# Revit family: TopVent_TC
name_source: partatom
category: Mechanical Equipment
revit_build: Autodesk Revit MEP 2015 (Build: 20160512_0715(x64)
units: mm (PartAtom-declared; Revit-internal decimal feet)

## types (3) — shared parameters
COBIE Connected load = 1.5 kW
COBIE Current consumption max. = 2.9A
COBIE Extract air temperature max. = 50°C
COBIE Floor area covered = 537.0
COBIE Frequency = 50 Hz
COBIE Nominal air flow rate = 6000.0
COBIE Octave sound power level - 1000 Hz = 74 dB
COBIE Octave sound power level - 125 Hz = 60 dB
COBIE Octave sound power level - 2000 Hz = 70 dB
COBIE Octave sound power level - 250 Hz = 65 dB
COBIE Octave sound power level - 4000 Hz = 64 dB
COBIE Octave sound power level - 500 Hz = 70 dB
COBIE Octave sound power level - 63 Hz = 55 dB
COBIE Octave sound power level - 8000 Hz = 56 dB
COBIE Permitted voltage tolerance = +/-5%
COBIE Pressure of the heating medium max. = 800 kPa
COBIE Protection rating = IP 54
COBIE Series fuse = 13A
COBIE Sound pressure level (at a distance of 5 m) = 55 dB(A)
COBIE Static efficiency of the fans = 48.5%
COBIE Supply air temperature max. = 60°C
COBIE Supply voltage = 3x400 V AC
COBIE Temperature of the heating medium max. = 90°C
COBIE Total sound power level = 77 dB(A)
Connected load = 3.6 kW
Current consumption max. = 5.9A
Extract air temperature max. = 50°C
Frequency = 50 Hz
M = 25 mm  [stored 0.082021 ft]
Permitted voltage tolerance = +/-5%
Pressure of the heating medium max. = 800 kPa
Protection rating = IP 54
Series fuse = 13A
Supply air temperature max. = 60°C
Supply voltage = 3x400 V AC
Temperature of the heating medium max. = 90°C

## per-type parameters (varying)
- TC-6-C: (X)=850 mm  [stored 2.78871 ft]; A=900 mm  [stored 2.95276 ft]; Air flow rate=3100 m3/h; B=1344 mm  [stored 4.40945 ft]; COBIE Air flow rate=3100 m3/h; COBIE Condensate quantity=90 kg/h; COBIE Condensate quantity 22 °C (50/70 %) - 6/12 °C=0.0/13.5 kg/h; COBIE Condensate quantity 22 °C (50/70 %) - 8/14 °C=0.0/7.9 kg/h; COBIE Condensate quantity 26 °C (50/70 %) - 6/12 °C=8.6/30.2 kg/h; COBIE Condensate quantity 26 °C (50/70 %) - 8/14 °C=3.0/24.6 kg/h; COBIE Effective electric power input=0.46 kW; COBIE Heat output 16/20 °C (60/40 °C)=18.8/16.2 kW; COBIE Heat output 16/20 °C (80/60 °C)=32.8/30.3 kW; COBIE Maximum mounting height 16/20 °C (60/40 °C)=16.8/17.9 m; COBIE Maximum mounting height 16/20 °C (80/60 °C)=13.4/14.0 m; COBIE Sensible cooling capacity 22 °C (50/70 %) - 6/12 °C=20.4/18.5 kW; COBIE Sensible cooling capacity 22 °C (50/70 %) - 8/14 °C=18.0/16.0 kW; COBIE Sensible cooling capacity 26 °C (50/70 %) - 6/12 °C=25.2/23.2 kW; COBIE Sensible cooling capacity 26 °C (50/70 %) - 8/14 °C=22.7/20.8 kW; COBIE Supply air temperature 16/20 °C (60/40 °C)=27.3/30.0 °C; COBIE Supply air temperature 16/20 °C (80/60 °C)=34.2/37.0 °C; COBIE Supply air temperature 22 °C (50/70 %) - 6/12 °C=13.9/14.9 °C; COBIE Supply air temperature 22 °C (50/70 %) - 8/14 °C=15.1/16.1 °C; COBIE Supply air temperature 26 °C (50/70 %) - 6/12 °C=15.5/16.5 °C; COBIE Supply air temperature 26 °C (50/70 %) - 8/14 °C=16.7/17.7 °C; COBIE Total cooling capacity 22 °C (50/70 %) - 6/12 °C=20.4/27.7 kW; COBIE Total cooling capacity 22 °C (50/70 %) - 8/14 °C=18.0/21.4 kW; COBIE Total cooling capacity 26 °C (50/70 %) - 6/12 °C=31.1/43.7 kW; COBIE Total cooling capacity 26 °C (50/70 %) - 8/14 °C=24.8/37.5 kW; COBIE Water content of heating/cooling coil=4.6 l; COBIE Water pressure drop 16/20 °C (60/40 °C)=2/2 kPa; COBIE Water pressure drop 16/20 °C (80/60 °C)=7/6 kPa; COBIE Water pressure drop 22 °C (50/70 %) - 6/12 °C=15/28 kPa; COBIE Water pressure drop 22 °C (50/70 %) - 8/14 °C=12/17 kPa; COBIE Water pressure drop 26 °C (50/70 %) - 6/12 °C=36/71 kPa; COBIE Water pressure drop 26 °C (50/70 %) - 8/14 °C=23/52 kPa; COBIE Water quantity 16/20 °C (60/40 °C)=807/697 l/h; COBIE Water quantity 16/20 °C (80/60 °C)=1410/1301 l/h; COBIE Water quantity 22 °C (50/70 %) - 6/12 °C=2925/3960 l/h; COBIE Water quantity 22 °C (50/70 %) - 8/14 °C=2573/3064 l/h; COBIE Water quantity 26 °C (50/70 %) - 6/12 °C=4448/6263 l/h; COBIE Water quantity 26 °C (50/70 %) - 8/14 °C=3552/5367 l/h; COBIE Weight=104 kg; Condensate quantity=90 kg/h; Condensate quantity 22 °C (50/70 %) - 6/12 °C=0.0/13.5 kg/h; Condensate quantity 22 °C (50/70 %) - 8/14 °C=0.0/7.9 kg/h; Condensate quantity 26 °C (50/70 %) - 6/12 °C=8.6/30.2 kg/h; Condensate quantity 26 °C (50/70 %) - 8/14 °C=3.0/24.6 kg/h; E=594 mm  [stored 1.94882 ft]; E/2=297 mm  [stored 0.974409 ft]; Effective electric power input=0.67 kW; F=758 mm  [stored 2.48688 ft]; Floor area covered=537 m²; G=77 mm  [stored 0.252625 ft]; H=155 mm  [stored 0.50853 ft]; Heat output 16/20 °C (60/40 °C)=45.0/39.3 kW; Heat output 16/20 °C (80/60 °C)=76.0/70.3 kW; I=760 mm  [stored 2.49344 ft]; J=32 mm; K=521 mm  [stored 1.70932 ft]; Maximum mounting height 16/20 °C (60/40 °C)=11.8/12.5 m; Maximum mounting height 16/20 °C (80/60 °C)=9.4/9.8 m; N=1030 mm  [stored 3.37927 ft]; Nominal air flow rate=6000 m³/h; Octave sound power level - 1000 Hz=67 dB; Octave sound power level - 125 Hz=59 dB; Octave sound power level - 2000 Hz=67 dB; Octave sound power level - 250 Hz=62 dB; Octave sound power level - 4000 Hz=66 dB; Octave sound power level - 500 Hz=65 dB; Octave sound power level - 63 Hz=41 dB; Octave sound power level - 8000 Hz=61 dB; R=1375 mm  [stored 4.51115 ft]; Sensible cooling capacity 22 °C (50/70 %) - 6/12 °C=20.4/18.5 kW; Sensible cooling capacity 22 °C (50/70 %) - 8/14 °C=18.0/16.0 kW; Sensible cooling capacity 26 °C (50/70 %) - 6/12 °C=25.2/23.2 kW; Sensible cooling capacity 26 °C (50/70 %) - 8/14 °C=22.7/20.8 kW; Sound pressure level (at a distance of 5 m)=51 dB(A); Static efficiency of the fans=63.6%; Supply air temperature 16/20 °C (60/40 °C)=40.3/41.5 °C; Supply air temperature 16/20 °C (80/60 °C)=55.6/56.8 °C; Supply air temperature 22 °C (50/70 %) - 6/12 °C=13.9/14.9 °C; Supply air temperature 22 °C (50/70 %) - 8/14 °C=15.1/16.1 °C; Supply air temperature 26 °C (50/70 %) - 6/12 °C=15.5/16.5 °C; Supply air temperature 26 °C (50/70 %) - 8/14 °C=16.7/17.7 °C; Total cooling capacity 22 °C (50/70 %) - 6/12 °C=20.4/27.7 kW; Total cooling capacity 22 °C (50/70 %) - 8/14 °C=18.0/21.4 kW; Total cooling capacity 26 °C (50/70 %) - 6/12 °C=31.1/43.7 kW; Total cooling capacity 26 °C (50/70 %) - 8/14 °C=24.8/37.5 kW; Total sound power level=73 dB(A); Water content of heating/cooling coil=7.9 l; Water pressure drop 16/20 °C (60/40 °C)=6/5 kPa; Water pressure drop 16/20 °C (80/60 °C)=18/16 kPa; Water pressure drop 22 °C (50/70 %) - 6/12 °C=15/28 kPa; Water pressure drop 22 °C (50/70 %) - 8/14 °C=12/17 kPa; Water pressure drop 26 °C (50/70 %) - 6/12 °C=36/71 kPa; Water pressure drop 26 °C (50/70 %) - 8/14 °C=23/52 kPa; Water quantity 16/20 °C (60/40 °C)=1935/1690 l/h; Water quantity 16/20 °C (80/60 °C)=3267/3022 l/h; Water quantity 22 °C (50/70 %) - 6/12 °C=2925/3960 l/h; Water quantity 22 °C (50/70 %) - 8/14 °C=2573/3064 l/h; Water quantity 26 °C (50/70 %) - 6/12 °C=4448/6263 l/h; Water quantity 26 °C (50/70 %) - 8/14 °C=3552/5367 l/h; Weight=216 kg
- TC-9-C: (X)=930 mm  [stored 3.05118 ft]; A=1100 mm; Air flow rate=5000 m3/h; B=1430 mm  [stored 4.6916 ft]; COBIE Air flow rate=5000 m3/h; COBIE Condensate quantity=150 kg/h; COBIE Condensate quantity 22 °C (50/70 %) - 6/12 °C=0.0/23.9 kg/h; COBIE Condensate quantity 22 °C (50/70 %) - 8/14 °C=0.0/5.2 kg/h; COBIE Condensate quantity 26 °C (50/70 %) - 6/12 °C=16.3/49.8 kg/h; COBIE Condensate quantity 26 °C (50/70 %) - 8/14 °C=0.0/31.1 kg/h; COBIE Effective electric power input=0.53 kW; COBIE Heat output 16/20 °C (60/40 °C)=26.9/23.3 kW; COBIE Heat output 16/20 °C (80/60 °C)=47.0/43.4 kW; COBIE Maximum mounting height 16/20 °C (60/40 °C)=14.6/15.5 m; COBIE Maximum mounting height 16/20 °C (80/60 °C)=11.6/12.0 m; COBIE Sensible cooling capacity 22 °C (50/70 %) - 6/12 °C=31.4/28.4 kW; COBIE Sensible cooling capacity 22 °C (50/70 %) - 8/14 °C=27.6/24.6 kW; COBIE Sensible cooling capacity 26 °C (50/70 %) - 6/12 °C=38.8/35.9 kW; COBIE Sensible cooling capacity 26 °C (50/70 %) - 8/14 °C=35.0/32.0 kW; COBIE Supply air temperature 16/20 °C (60/40 °C)=31.1/33.5 °C; COBIE Supply air temperature 16/20 °C (80/60 °C)=41.3/43.5 °C; COBIE Supply air temperature 22 °C (50/70 %) - 6/12 °C=13.6/14.6 °C; COBIE Supply air temperature 22 °C (50/70 %) - 8/14 °C=14.9/15.9 °C; COBIE Supply air temperature 26 °C (50/70 %) - 6/12 °C=15.2/16.2 °C; COBIE Supply air temperature 26 °C (50/70 %) - 8/14 °C=16.4/17.4 °C; COBIE Total cooling capacity 22 °C (50/70 %) - 6/12 °C=31.4/44.7 kW; COBIE Total cooling capacity 22 °C (50/70 %) - 8/14 °C=27.6/28.2 kW; COBIE Total cooling capacity 26 °C (50/70 %) - 6/12 °C=49.9/69.8 kW; COBIE Total cooling capacity 26 °C (50/70 %) - 8/14 °C=35.0/53.2 kW; COBIE Water content of heating/cooling coil=4.6 l; COBIE Water pressure drop 16/20 °C (60/40 °C)=4/3 kPa; COBIE Water pressure drop 16/20 °C (80/60 °C)=13/11 kPa; COBIE Water pressure drop 22 °C (50/70 %) - 6/12 °C=15/31 kPa; COBIE Water pressure drop 22 °C (50/70 %) - 8/14 °C=12/12 kPa; COBIE Water pressure drop 26 °C (50/70 %) - 6/12 °C=38/75 kPa; COBIE Water pressure drop 26 °C (50/70 %) - 8/14 °C=19/44 kPa; COBIE Water quantity 16/20 °C (60/40 °C)=1157/1001 l/h; COBIE Water quantity 16/20 °C (80/60 °C)=2020/1864 l/h; COBIE Water quantity 22 °C (50/70 %) - 6/12 °C=4496/6401 l/h; COBIE Water quantity 22 °C (50/70 %) - 8/14 °C=3947/4031 l/h; COBIE Water quantity 26 °C (50/70 %) - 6/12 °C=7149/9989 l/h; COBIE Water quantity 26 °C (50/70 %) - 8/14 °C=5013/7619 l/h; COBIE Weight=104 kg; Condensate quantity=150 kg/h; Condensate quantity 22 °C (50/70 %) - 6/12 °C=0.0/23.9 kg/h; Condensate quantity 22 °C (50/70 %) - 8/14 °C=0.0/5.2 kg/h; Condensate quantity 26 °C (50/70 %) - 6/12 °C=16.3/49.8 kg/h; Condensate quantity 26 °C (50/70 %) - 8/14 °C=0.0/31.1 kg/h; E=846 mm  [stored 2.77559 ft]; E/2=423 mm  [stored 1.3878 ft]; Effective electric power input=1.23 kW; F=882 mm  [stored 2.8937 ft]; Floor area covered=946 m²; G=93 mm  [stored 0.305118 ft]; H=171 mm  [stored 0.561024 ft]; Heat output 16/20 °C (60/40 °C)=69.9/61.0 kW; Heat output 16/20 °C (80/60 °C)=117.9/109.1 kW; I=935 mm; J=38 mm; K=558 mm; Maximum mounting height 16/20 °C (60/40 °C)=12.3/13.1 m; Maximum mounting height 16/20 °C (80/60 °C)=9.8/10.2 m; N=1230 mm  [stored 4.03543 ft]; Nominal air flow rate=9000 m³/h; Octave sound power level - 1000 Hz=75 dB; Octave sound power level - 125 Hz=67 dB; Octave sound power level - 2000 Hz=75 dB; Octave sound power level - 250 Hz=70 dB; Octave sound power level - 4000 Hz=74 dB; Octave sound power level - 500 Hz=73 dB; Octave sound power level - 63 Hz=49 dB; Octave sound power level - 8000 Hz=68 dB; R=1463 mm  [stored 4.79987 ft]; Sensible cooling capacity 22 °C (50/70 %) - 6/12 °C=31.4/28.4 kW; Sensible cooling capacity 22 °C (50/70 %) - 8/14 °C=27.6/24.6 kW; Sensible cooling capacity 26 °C (50/70 %) - 6/12 °C=38.8/35.9 kW; Sensible cooling capacity 26 °C (50/70 %) - 8/14 °C=35.0/32.0 kW; Sound pressure level (at a distance of 5 m)=59 dB(A); Static efficiency of the fans=63.3%; Supply air temperature 16/20 °C (60/40 °C)=41.1/42.1 °C; Supply air temperature 16/20 °C (80/60 °C)=56.9/58.0 °C; Supply air temperature 22 °C (50/70 %) - 6/12 °C=13.6/14.6 °C; Supply air temperature 22 °C (50/70 %) - 8/14 °C=14.9/15.9 °C; Supply air temperature 26 °C (50/70 %) - 6/12 °C=15.2/16.2 °C; Supply air temperature 26 °C (50/70 %) - 8/14 °C=16.4/17.4 °C; Total cooling capacity 22 °C (50/70 %) - 6/12 °C=31.4/44.7 kW; Total cooling capacity 22 °C (50/70 %) - 8/14 °C=27.6/28.2 kW; Total cooling capacity 26 °C (50/70 %) - 6/12 °C=49.9/69.8 kW; Total cooling capacity 26 °C (50/70 %) - 8/14 °C=35.0/53.2 kW; Total sound power level=81 dB(A); Water content of heating/cooling coil=12.4 l; Water pressure drop 16/20 °C (60/40 °C)=6/5 kPa; Water pressure drop 16/20 °C (80/60 °C)=18/15 kPa; Water pressure drop 22 °C (50/70 %) - 6/12 °C=15/31 kPa; Water pressure drop 22 °C (50/70 %) - 8/14 °C=12/12 kPa; Water pressure drop 26 °C (50/70 %) - 6/12 °C=38/75 kPa; Water pressure drop 26 °C (50/70 %) - 8/14 °C=19/44 kPa; Water quantity 16/20 °C (60/40 °C)=3003/2622 l/h; Water quantity 16/20 °C (80/60 °C)=5066/4686 l/h; Water quantity 22 °C (50/70 %) - 6/12 °C=4496/6401 l/h; Water quantity 22 °C (50/70 %) - 8/14 °C=3947/4031 l/h; Water quantity 26 °C (50/70 %) - 6/12 °C=7149/9989 l/h; Water quantity 26 °C (50/70 %) - 8/14 °C=5013/7619 l/h; Weight=265 kg
- TC-9-D: (X)=930 mm  [stored 3.05118 ft]; A=1100 mm; Air flow rate=5000 m3/h; B=1430 mm  [stored 4.6916 ft]; COBIE Air flow rate=5000 m3/h; COBIE Condensate quantity=150 kg/h; COBIE Condensate quantity 22 °C (50/70 %) - 6/12 °C=0.0/32.5 kg/h; COBIE Condensate quantity 22 °C (50/70 %) - 8/14 °C=0.0/22.6 kg/h; COBIE Condensate quantity 26 °C (50/70 %) - 6/12 °C=23.5/63.9 kg/h; COBIE Condensate quantity 26 °C (50/70 %) - 8/14 °C=13.6/54.0 kg/h; COBIE Effective electric power input=0.74 kW; COBIE Heat output 16/20 °C (60/40 °C)=45.0/39.3 kW; COBIE Heat output 16/20 °C (80/60 °C)=76.0/70.3 kW; COBIE Maximum mounting height 16/20 °C (60/40 °C)=11.8/12.5 m; COBIE Maximum mounting height 16/20 °C (80/60 °C)=9.4/9.8 m; COBIE Sensible cooling capacity 22 °C (50/70 %) - 6/12 °C=37.1/34.6 kW; COBIE Sensible cooling capacity 22 °C (50/70 %) - 8/14 °C=32.2/29.7 kW; COBIE Sensible cooling capacity 26 °C (50/70 %) - 6/12 °C=46.4/43.9 kW; COBIE Sensible cooling capacity 26 °C (50/70 %) - 8/14 °C=41.6/39.1 kW; COBIE Supply air temperature 16/20 °C (60/40 °C)=40.3/41.5 °C; COBIE Supply air temperature 16/20 °C (80/60 °C)=55.6/56.8 °C; COBIE Supply air temperature 22 °C (50/70 %) - 6/12 °C=11.8/12.6 °C; COBIE Supply air temperature 22 °C (50/70 %) - 8/14 °C=13.4/14.2 °C; COBIE Supply air temperature 26 °C (50/70 %) - 6/12 °C=12.7/13.5 °C; COBIE Supply air temperature 26 °C (50/70 %) - 8/14 °C=14.3/15.1 °C; COBIE Total cooling capacity 22 °C (50/70 %) - 6/12 °C=37.1/56.7 kW; COBIE Total cooling capacity 22 °C (50/70 %) - 8/14 °C=32.2/45.1 kW; COBIE Total cooling capacity 26 °C (50/70 %) - 6/12 °C=62.4/87.4 kW; COBIE Total cooling capacity 26 °C (50/70 %) - 8/14 °C=50.9/75.8 kW; COBIE Water content of heating/cooling coil=7.9 l; COBIE Water pressure drop 16/20 °C (60/40 °C)=6/5 kPa; COBIE Water pressure drop 16/20 °C (80/60 °C)=18/16 kPa; COBIE Water pressure drop 22 °C (50/70 %) - 6/12 °C=13/30 kPa; COBIE Water pressure drop 22 °C (50/70 %) - 8/14 °C=10/19 kPa; COBIE Water pressure drop 26 °C (50/70 %) - 6/12 °C=36/70 kPa; COBIE Water pressure drop 26 °C (50/70 %) - 8/14 °C=24/53 kPa; COBIE Water quantity 16/20 °C (60/40 °C)=1935/1690 l/h; COBIE Water quantity 16/20 °C (80/60 °C)=3267/3022 l/h; COBIE Water quantity 22 °C (50/70 %) - 6/12 °C=5307/8118 l/h; COBIE Water quantity 22 °C (50/70 %) - 8/14 °C=4613/6459 l/h; COBIE Water quantity 26 °C (50/70 %) - 6/12 °C=8941/12513 l/h; COBIE Water quantity 26 °C (50/70 %) - 8/14 °C=7282/10854 l/h; COBIE Weight=111 kg; Condensate quantity=150 kg/h; Condensate quantity 22 °C (50/70 %) - 6/12 °C=0.0/32.5 kg/h; Condensate quantity 22 °C (50/70 %) - 8/14 °C=0.0/22.6 kg/h; Condensate quantity 26 °C (50/70 %) - 6/12 °C=23.5/63.9 kg/h; Condensate quantity 26 °C (50/70 %) - 8/14 °C=13.6/54.0 kg/h; E=846 mm  [stored 2.77559 ft]; E/2=423 mm  [stored 1.3878 ft]; Effective electric power input=1.34 kW; F=882 mm  [stored 2.8937 ft]; Floor area covered=946 m²; G=85 mm  [stored 0.278871 ft]; H=180 mm  [stored 0.590551 ft]; Heat output 16/20 °C (60/40 °C)=85.4/75.1 kW; Heat output 16/20 °C (80/60 °C)=140.7/130.4 kW; I=935 mm; J=51 mm; K=558 mm; Maximum mounting height 16/20 °C (60/40 °C)=11.3/12.0 m; Maximum mounting height 16/20 °C (80/60 °C)=9.1/9.5 m; N=1230 mm  [stored 4.03543 ft]; Nominal air flow rate=9000 m³/h; Octave sound power level - 1000 Hz=75 dB; Octave sound power level - 125 Hz=67 dB; Octave sound power level - 2000 Hz=75 dB; Octave sound power level - 250 Hz=70 dB; Octave sound power level - 4000 Hz=74 dB; Octave sound power level - 500 Hz=73 dB; Octave sound power level - 63 Hz=49 dB; Octave sound power level - 8000 Hz=68 dB; R=1463 mm  [stored 4.79987 ft]; Sensible cooling capacity 22 °C (50/70 %) - 6/12 °C=37.1/34.6 kW; Sensible cooling capacity 22 °C (50/70 %) - 8/14 °C=32.2/29.7 kW; Sensible cooling capacity 26 °C (50/70 %) - 6/12 °C=46.4/43.9 kW; Sensible cooling capacity 26 °C (50/70 %) - 8/14 °C=41.6/39.1 kW; Sound pressure level (at a distance of 5 m)=59 dB(A); Static efficiency of the fans=63.3%; Supply air temperature 16/20 °C (60/40 °C)=46.2/46.8 °C; Supply air temperature 16/20 °C (80/60 °C)=64.4/65.0 °C; Supply air temperature 22 °C (50/70 %) - 6/12 °C=11.8/12.6 °C; Supply air temperature 22 °C (50/70 %) - 8/14 °C=13.4/14.2 °C; Supply air temperature 26 °C (50/70 %) - 6/12 °C=12.7/13.5 °C; Supply air temperature 26 °C (50/70 %) - 8/14 °C=14.3/15.1 °C; Total cooling capacity 22 °C (50/70 %) - 6/12 °C=37.1/56.7 kW; Total cooling capacity 22 °C (50/70 %) - 8/14 °C=32.2/45.1 kW; Total cooling capacity 26 °C (50/70 %) - 6/12 °C=62.4/87.4 kW; Total cooling capacity 26 °C (50/70 %) - 8/14 °C=50.9/75.8 kW; Total sound power level=81 dB(A); Water content of heating/cooling coil=19.2 l; Water pressure drop 16/20 °C (60/40 °C)=5/4 kPa; Water pressure drop 16/20 °C (80/60 °C)=15/13 kPa; Water pressure drop 22 °C (50/70 %) - 6/12 °C=13/30 kPa; Water pressure drop 22 °C (50/70 %) - 8/14 °C=10/19 kPa; Water pressure drop 26 °C (50/70 %) - 6/12 °C=36/70 kPa; Water pressure drop 26 °C (50/70 %) - 8/14 °C=24/53 kPa; Water quantity 16/20 °C (60/40 °C)=3670/3225 l/h; Water quantity 16/20 °C (80/60 °C)=6045/5600 l/h; Water quantity 22 °C (50/70 %) - 6/12 °C=5307/8118 l/h; Water quantity 22 °C (50/70 %) - 8/14 °C=4613/6459 l/h; Water quantity 26 °C (50/70 %) - 6/12 °C=8941/12513 l/h; Water quantity 26 °C (50/70 %) - 8/14 °C=7282/10854 l/h; Weight=276 kg

note: [stored X ft] marks values corroborated as IEEE doubles in the binary element streams (Revit-internal decimal feet)

## geometry (parser evidence)
native form markers: Sweep x7
no freeform markers — native parametric forms only
